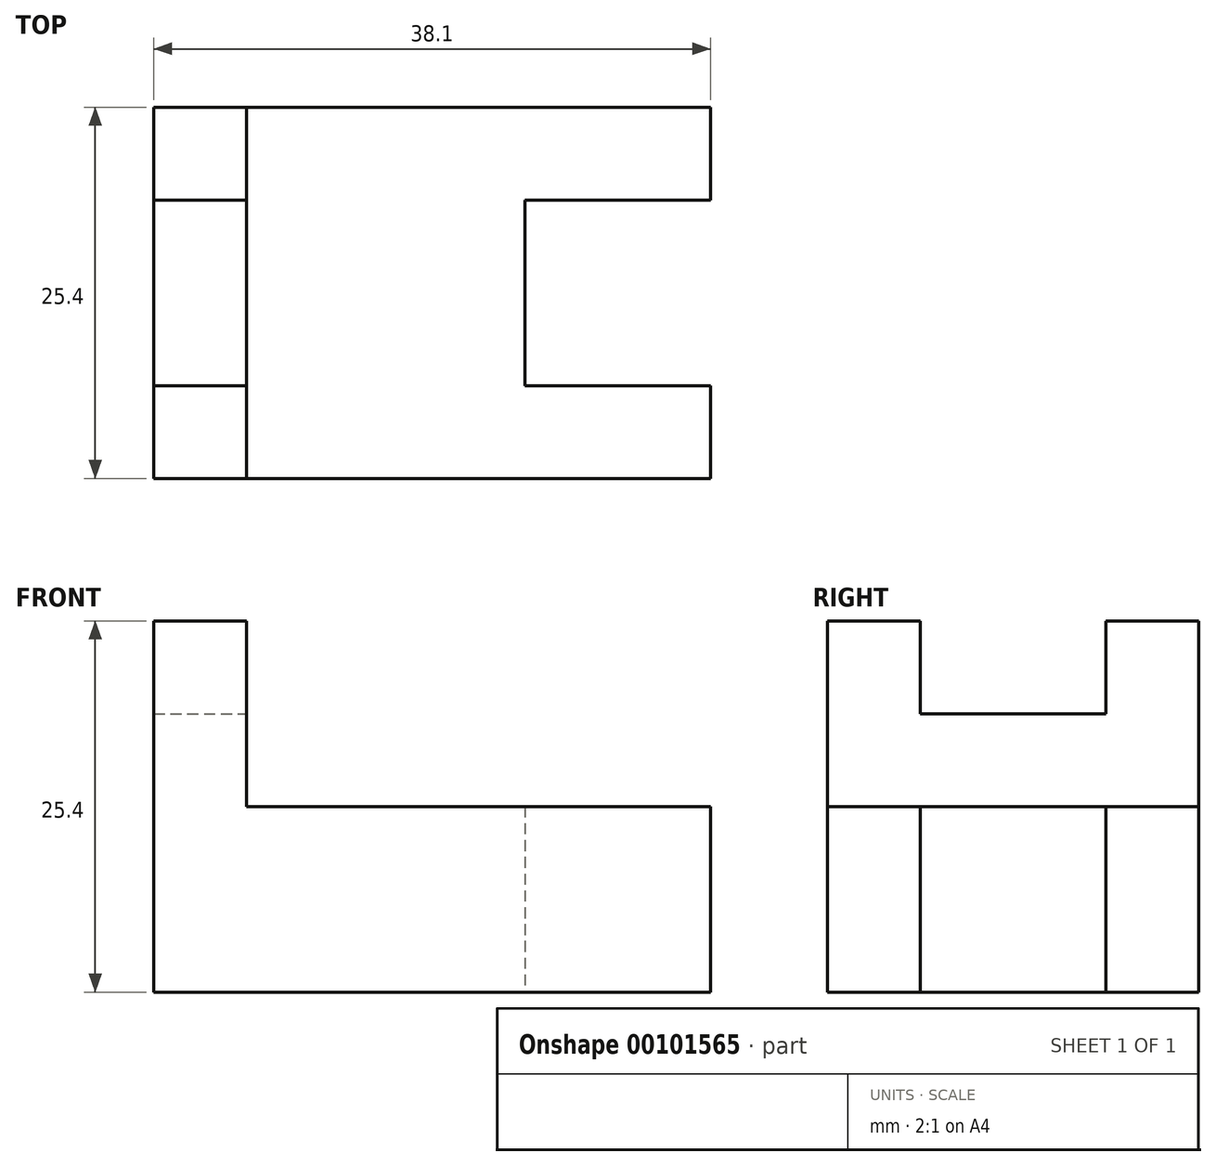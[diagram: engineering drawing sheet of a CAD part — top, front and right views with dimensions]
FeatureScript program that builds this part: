
annotation { "Feature Type Name" : "Feature", "Feature Type Description" : "" }
export const myFeature = defineFeature(function(context is Context, id is Id, definition is map)
    precondition{}
    {
        {
            var Q0;
            Q0=qCreatedBy(makeId("Front.planeOp"),FACE);
            var sketch = newSketch(context, id + "F0", { "sketchPlane" : qUnion([Q0])});
            skLineSegment(sketch, "E0", {"start": v(0, 0) * mm, "end": v(0, 25.4) * mm});
            skLineSegment(sketch, "E1", {"start": v(0, 25.4) * mm, "end": v(6.35, 25.4) * mm});
            skLineSegment(sketch, "E2", {"start": v(6.35, 25.4) * mm, "end": v(6.35, 12.7) * mm});
            skLineSegment(sketch, "E3", {"start": v(6.35, 12.7) * mm, "end": v(38.1, 12.7) * mm});
            skLineSegment(sketch, "E4", {"start": v(38.1, 12.7) * mm, "end": v(38.1, 0) * mm});
            skLineSegment(sketch, "E5", {"start": v(38.1, 0) * mm, "end": v(0, 0) * mm});
            skSolve(sketch);
        }
        {
            var Q0;
            Q0 = qSketchRegion(id + "F0", true);
            extrude(context, id + "F1", {"entities" : qUnion([Q0]), "endBound" : BoundingType.SYMMETRIC, "depth" : 25.4 * mm});
        }
        {
            var Q0;
            Q0=qCreatedBy(makeId("Front.planeOp"),FACE);
            var sketch = newSketch(context, id + "F2", { "sketchPlane" : qUnion([Q0])});
            skLineSegment(sketch, "E6.bottom", {"start": v(0, 25.4) * mm, "end": v(6.35, 25.4) * mm});
            skLineSegment(sketch, "E6.top", {"start": v(0, 19.05) * mm, "end": v(6.35, 19.05) * mm});
            skLineSegment(sketch, "E6.left", {"start": v(0, 25.4) * mm, "end": v(0, 19.05) * mm});
            skLineSegment(sketch, "E6.right", {"start": v(6.35, 25.4) * mm, "end": v(6.35, 19.05) * mm});
            skSolve(sketch);
        }
        {
            var Q0;
            Q0 = qSketchRegion(id + "F2", true);
            extrude(context, id + "F3", {"entities" : qUnion([Q0]), "operationType" : NewBodyOperationType.REMOVE, "endBound" : BoundingType.SYMMETRIC, "oppositeDirection" : true, "depth" : 12.7 * mm});
        }
        {
            var Q0;
            Q0=qCreatedBy(makeId("Front.planeOp"),FACE);
            var sketch = newSketch(context, id + "F4", { "sketchPlane" : qUnion([Q0])});
            skLineSegment(sketch, "E7.bottom", {"start": v(25.4, 12.7) * mm, "end": v(38.1, 12.7) * mm});
            skLineSegment(sketch, "E7.top", {"start": v(25.4, 0) * mm, "end": v(38.1, 0) * mm});
            skLineSegment(sketch, "E7.left", {"start": v(25.4, 12.7) * mm, "end": v(25.4, 0) * mm});
            skLineSegment(sketch, "E7.right", {"start": v(38.1, 12.7) * mm, "end": v(38.1, 0) * mm});
            skSolve(sketch);
        }
        {
            var Q0;
            Q0 = qSketchRegion(id + "F4", true);
            extrude(context, id + "F5", {"entities" : qUnion([Q0]), "operationType" : NewBodyOperationType.REMOVE, "endBound" : BoundingType.SYMMETRIC, "depth" : 12.7 * mm});
        }
    });
